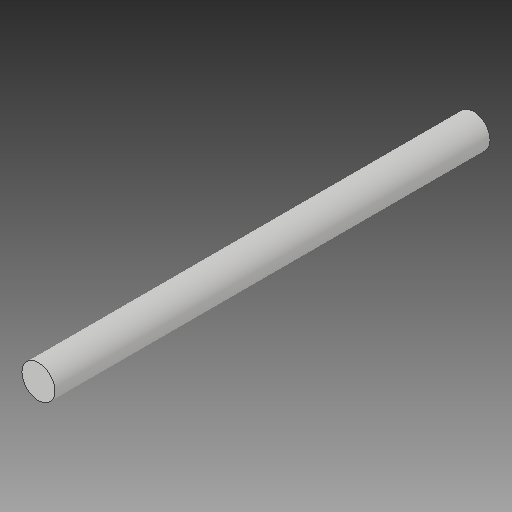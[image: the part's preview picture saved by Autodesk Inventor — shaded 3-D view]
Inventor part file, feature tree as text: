
AUTODESK INVENTOR PART (.ipt)
format: ipt  version: 2019 (Build 230136000, 136)  size: 90,624 bytes
history: native  units: mm
features: extrude x1, sketch x1
ambient origin geometry x8: Origin, YZ Plane, XZ Plane, XY Plane, X Axis, Y Axis, Z Axis, Center Point
bodies: Solid1 (feature_tree)
feature tree (2):
  extrude  "Extrusion1"  Depth=92.0mm TaperAngle=0.0deg
  sketch  "Sketch1"  dims[d0=7.0mm d1=92.0mm d2=0.0mm]
